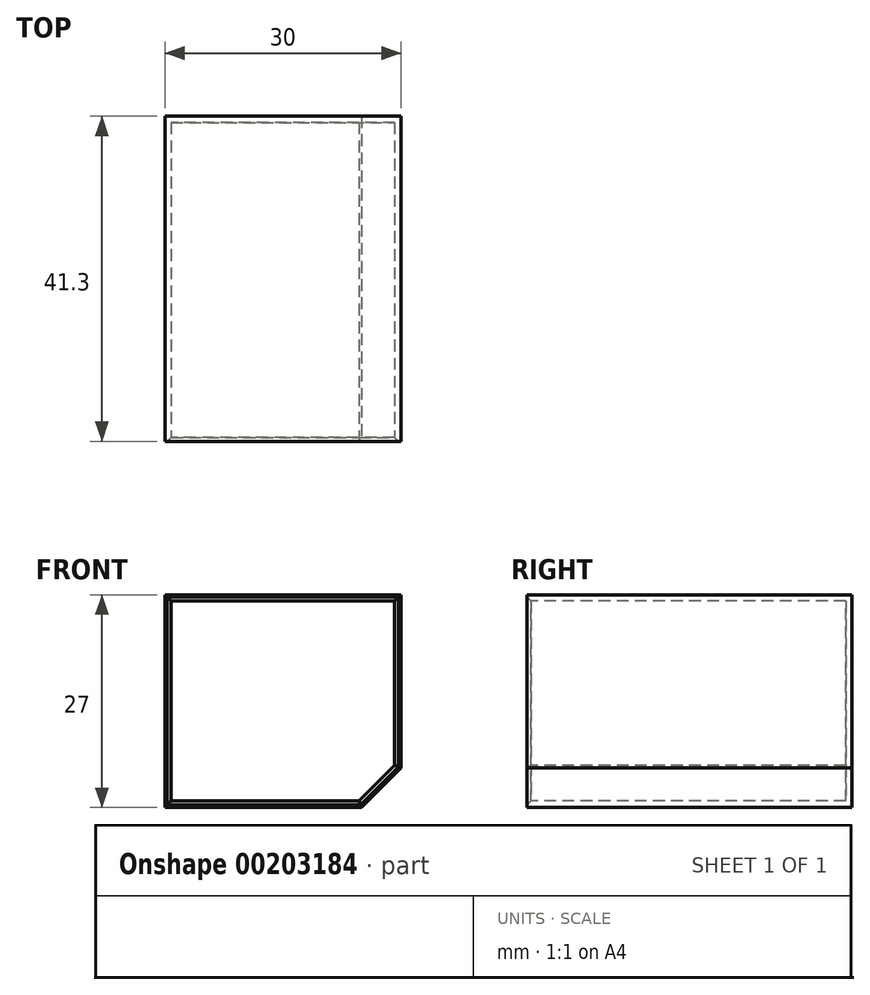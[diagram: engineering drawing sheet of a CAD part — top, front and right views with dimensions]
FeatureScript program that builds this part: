
annotation { "Feature Type Name" : "Feature", "Feature Type Description" : "" }
export const myFeature = defineFeature(function(context is Context, id is Id, definition is map)
    precondition{}
    {
        {
            assignVariable(context, id + "F0", {"name" : "epparoi", "anyValue" : 0.8});
        }
        {
            var Q0;
            Q0=qCreatedBy(makeId("Front.planeOp"),FACE);
            var sketch = newSketch(context, id + "F1", { "sketchPlane" : qUnion([Q0])});
            skLineSegment(sketch, "E0", {"start": v(0, 0) * mm, "end": v(0, 27) * mm});
            skLineSegment(sketch, "E1", {"start": v(0, 27) * mm, "end": v(30, 27) * mm});
            skLineSegment(sketch, "E2", {"start": v(30, 27) * mm, "end": v(30, 5) * mm});
            skLineSegment(sketch, "E3", {"start": v(30, 5) * mm, "end": v(25, 0) * mm});
            skLineSegment(sketch, "E4", {"start": v(25, 0) * mm, "end": v(0, 0) * mm});
            skSolve(sketch);
        }
        {
            var Q0;
            Q0=makeQuery(id+"F1.imprint","IMPRINT",FACE,{"disambiguationData":[TD([[makeQuery(id+"F1.imprint","IMPRINT",EDGE,{"derivedFrom":sQuery(id+"F1.wireOp",EDGE,"E0")}),-1.0]])]});
            extrude(context, id + "F2", {"entities" : qUnion([Q0]), "oppositeDirection" : true, "depth" : 41.3 * mm});
        }
        {
            var Q0;
            Q0=makeQuery(id+"F2.opExtrude","CAP_FACE",FACE,{"disambiguationData":[OSD([sQuery(id+"F1.wireOp",EDGE,"E0"),sQuery(id+"F1.wireOp",EDGE,"E1"),sQuery(id+"F1.wireOp",EDGE,"E2"),sQuery(id+"F1.wireOp",EDGE,"E3"),sQuery(id+"F1.wireOp",EDGE,"E4")])],"isStart":true});
            shell(context, id + "F3", {"entities" : qUnion([Q0]), "thickness" : (getVariable(context, 'epparoi')) * mm});
        }
        {
            var Q0;
            {var subQ0=sQuery(id+"F1.wireOp",EDGE,"E1");Q0=makeQuery(id+"F3.opShell","OFFSET_EDGE",EDGE,{"disambiguationData":[OSD([subQ0]),TDD([makeQuery(id+"F2.opExtrude","CAP_EDGE",EDGE,{"disambiguationData":[OSD([subQ0])],"isStart":true})])]});}
            var Q1;
            {var subQ0=sQuery(id+"F1.wireOp",EDGE,"E2");Q1=makeQuery(id+"F3.opShell","OFFSET_EDGE",EDGE,{"disambiguationData":[OSD([subQ0]),TDD([makeQuery(id+"F2.opExtrude","CAP_EDGE",EDGE,{"disambiguationData":[OSD([subQ0])],"isStart":true})])]});}
            var Q2;
            {var subQ0=sQuery(id+"F1.wireOp",EDGE,"E3");Q2=makeQuery(id+"F3.opShell","OFFSET_EDGE",EDGE,{"disambiguationData":[OSD([subQ0]),TDD([makeQuery(id+"F2.opExtrude","CAP_EDGE",EDGE,{"disambiguationData":[OSD([subQ0])],"isStart":true})])]});}
            var Q3;
            {var subQ0=sQuery(id+"F1.wireOp",EDGE,"E4");Q3=makeQuery(id+"F3.opShell","OFFSET_EDGE",EDGE,{"disambiguationData":[OSD([subQ0]),TDD([makeQuery(id+"F2.opExtrude","CAP_EDGE",EDGE,{"disambiguationData":[OSD([subQ0])],"isStart":true})])]});}
            var Q4;
            {var subQ0=sQuery(id+"F1.wireOp",EDGE,"E0");Q4=makeQuery(id+"F3.opShell","OFFSET_EDGE",EDGE,{"disambiguationData":[OSD([subQ0]),TDD([makeQuery(id+"F2.opExtrude","CAP_EDGE",EDGE,{"disambiguationData":[OSD([subQ0])],"isStart":true})])]});}
            chamfer(context, id + "F4", {"entities" : qUnion([Q0, Q1, Q2, Q3, Q4]), "width" : 0.5 * mm, "tangentPropagation" : true});
        }
    });
